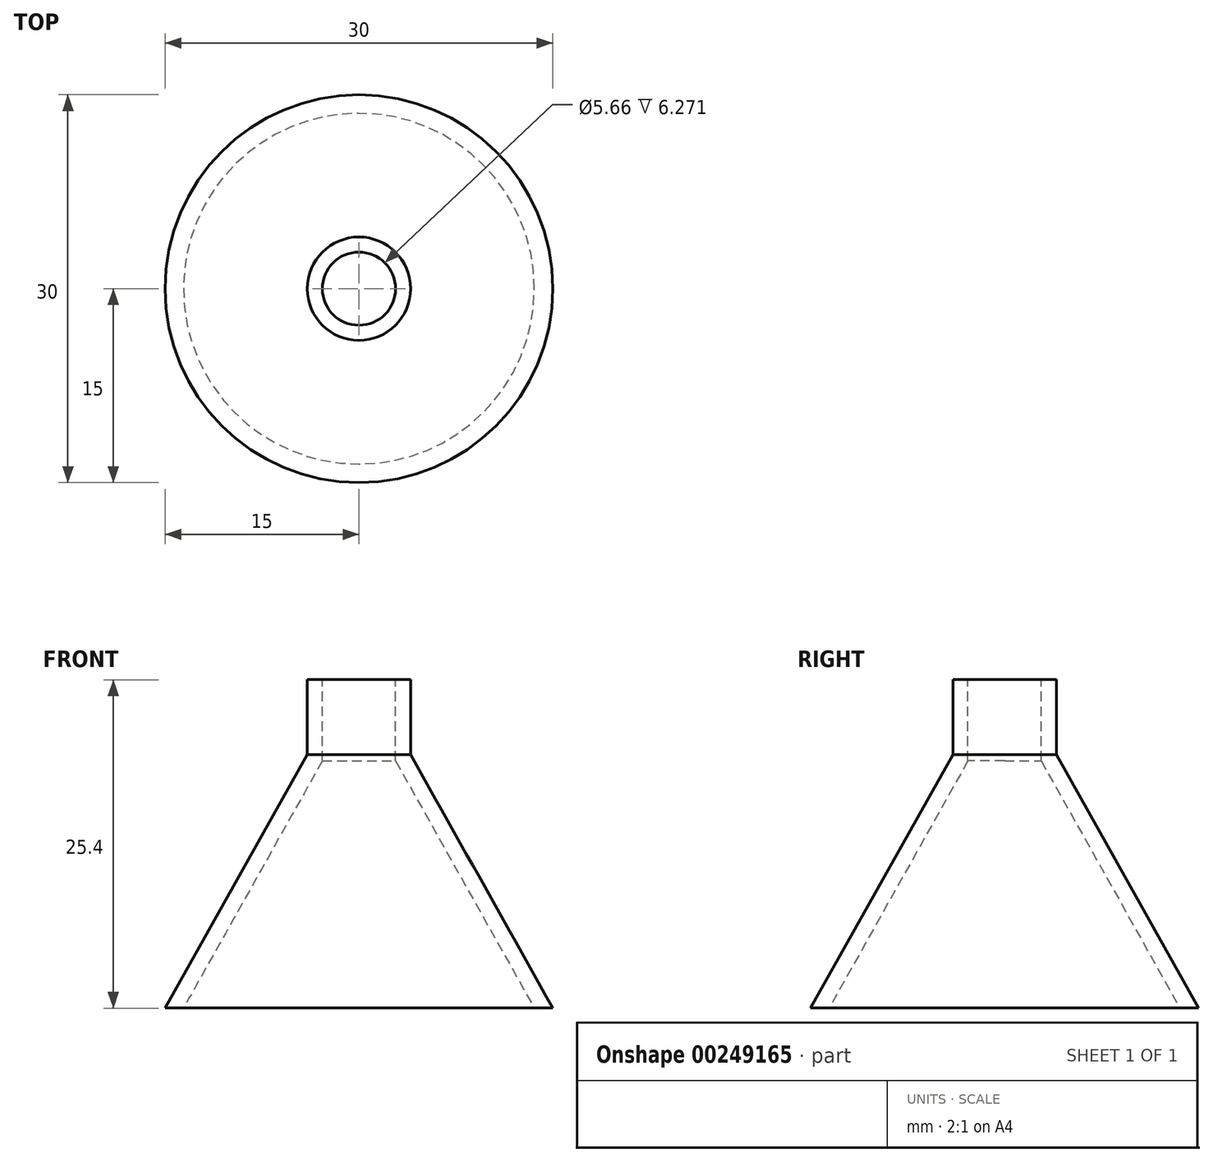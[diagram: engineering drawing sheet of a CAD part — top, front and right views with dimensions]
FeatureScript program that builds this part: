
annotation { "Feature Type Name" : "Feature", "Feature Type Description" : "" }
export const myFeature = defineFeature(function(context is Context, id is Id, definition is map)
    precondition{}
    {
        {
            var Q0;
            Q0=qCreatedBy(makeId("Front.planeOp"),FACE);
            var sketch = newSketch(context, id + "F0", { "sketchPlane" : qUnion([Q0])});
            skLineSegment(sketch, "E0", {"start": v(0, 12.91) * mm, "end": v(-4, 12.91) * mm});
            skLineSegment(sketch, "E1", {"start": v(-4, 12.91) * mm, "end": v(-4, 7.11) * mm});
            skLineSegment(sketch, "E2", {"start": v(-4, 7.11) * mm, "end": v(-15, -12.49) * mm});
            skLineSegment(sketch, "E3", {"start": v(-15, -12.49) * mm, "end": v(0, -12.49) * mm});
            skLineSegment(sketch, "E4", {"start": v(0, -12.49) * mm, "end": v(0, 12.91) * mm});
            skLineSegment(sketch, "E5", {"start": v(0, 27.91) * mm, "end": v(0, 15.48) * mm, "construction": true});
            skSolve(sketch);
        }
        {
            var Q0;
            Q0=makeQuery(id+"F0.imprint","IMPRINT",FACE,{"disambiguationData":[TD([[makeQuery(id+"F0.imprint","IMPRINT",EDGE,{"derivedFrom":sQuery(id+"F0.wireOp",EDGE,"E0")}),1.0]])]});
            var Q1;
            Q1=sQuery(id+"F0.wireOp",EDGE,"E5");
            revolve(context, id + "F1", {"entities" : qUnion([Q0]), "axis" : qUnion([Q1]), "revolveType" : RevolveType.FULL});
        }
        {
            var Q0;
            Q0=makeQuery(id+"F1.opRevolve","SWEPT_FACE",FACE,{"disambiguationData":[OSD([sQuery(id+"F0.wireOp",EDGE,"E3")])]});
            shell(context, id + "F2", {"entities" : qUnion([Q0]), "thickness" : 1.25 * mm});
        }
        {
            var Q0;
            Q0=makeQuery(id+"F1.opRevolve","SWEPT_FACE",FACE,{"disambiguationData":[OSD([sQuery(id+"F0.wireOp",EDGE,"E0")])]});
            var sketch = newSketch(context, id + "F3", { "sketchPlane" : qUnion([Q0])});
            skCircle(sketch, "E6", {"center": v(0, 0) * mm, "radius": 2.83 * mm});
            skSolve(sketch);
        }
        {
            var Q0;
            Q0 = qSketchRegion(id + "F3", true);
            extrude(context, id + "F4", {"entities" : qUnion([Q0]), "operationType" : NewBodyOperationType.REMOVE, "oppositeDirection" : true, "depth" : 25 * mm});
        }
    });
